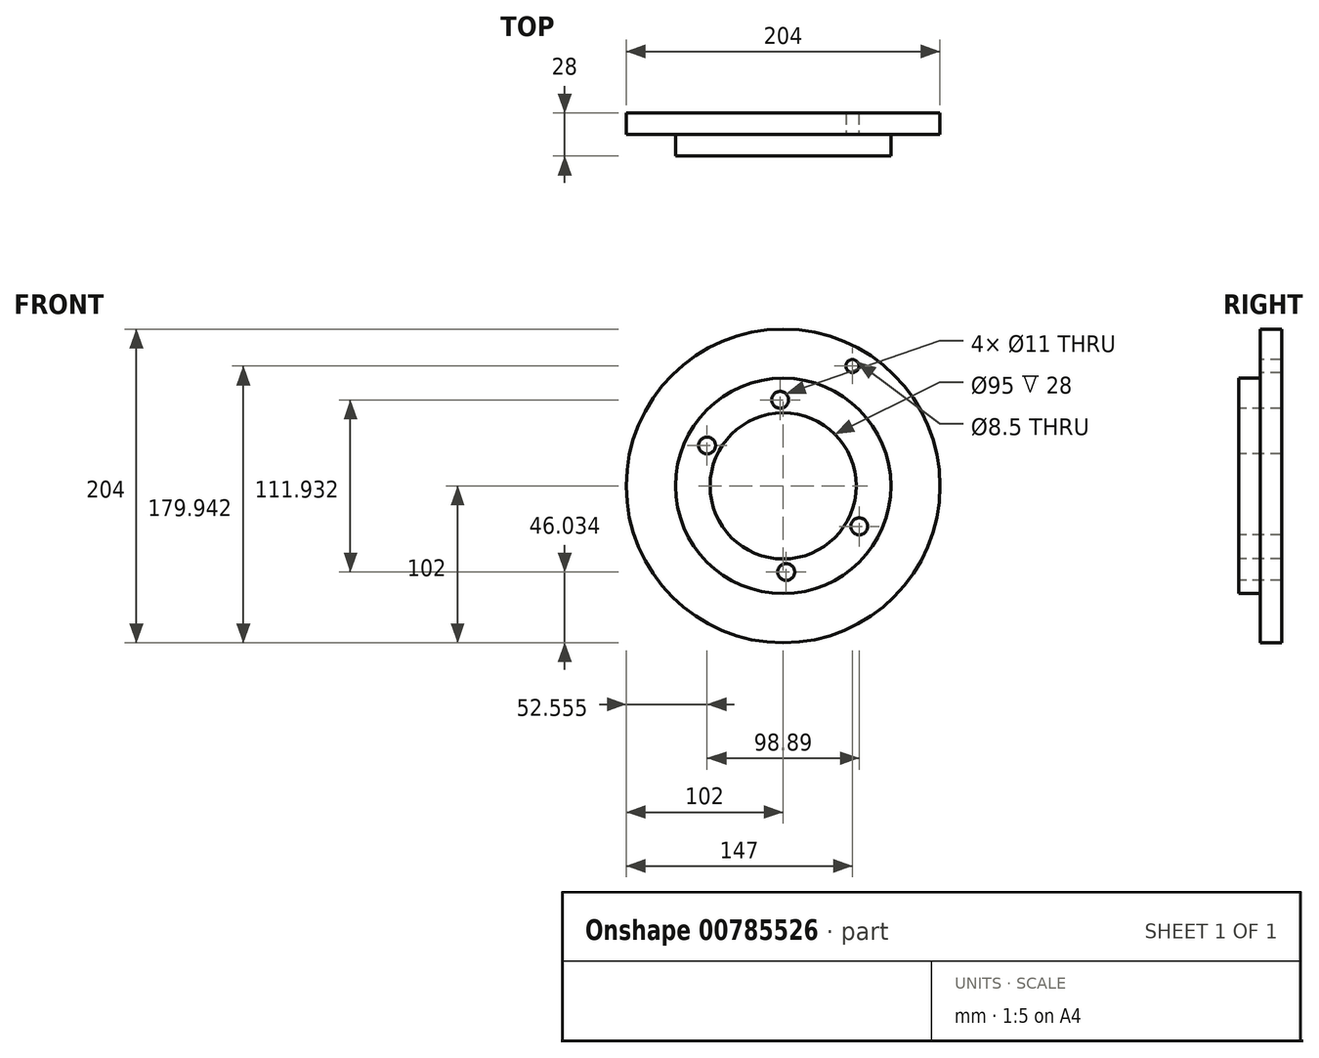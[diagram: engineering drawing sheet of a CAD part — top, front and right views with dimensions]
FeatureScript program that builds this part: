
annotation { "Feature Type Name" : "Feature", "Feature Type Description" : "" }
export const myFeature = defineFeature(function(context is Context, id is Id, definition is map)
    precondition{}
    {
        {
            var Q0;
            Q0=qCreatedBy(makeId("Front.planeOp"),FACE);
            var sketch = newSketch(context, id + "F0", { "sketchPlane" : qUnion([Q0])});
            skCircle(sketch, "E0", {"center": v(0, 0) * mm, "radius": 102 * mm});
            skSolve(sketch);
        }
        {
            var Q0;
            Q0=makeQuery(id+"F0.imprint","IMPRINT",FACE,{"disambiguationData":[TD([[makeQuery(id+"F0.imprint","IMPRINT",EDGE,{"derivedFrom":sQuery(id+"F0.wireOp",EDGE,"E0")}),1.0]])]});
            extrude(context, id + "F1", {"entities" : qUnion([Q0]), "depth" : 14 * mm, "offsetDistance" : 25 * mm});
        }
        {
            var Q0;
            Q0=makeQuery(id+"F1.opExtrude","CAP_FACE",FACE,{"disambiguationData":[OSD([sQuery(id+"F0.wireOp",EDGE,"E0")])],"isStart":false});
            var sketch = newSketch(context, id + "F2", { "sketchPlane" : qUnion([Q0])});
            skCircle(sketch, "E1", {"center": v(0, 0) * mm, "radius": 47.5 * mm});
            skSolve(sketch);
        }
        {
            var Q0;
            Q0=makeQuery(id+"F2.imprint","IMPRINT",FACE,{"disambiguationData":[TD([[makeQuery(id+"F2.imprint","IMPRINT",EDGE,{"derivedFrom":sQuery(id+"F2.wireOp",EDGE,"E1")}),1.0]])]});
            extrude(context, id + "F3", {"entities" : qUnion([Q0]), "operationType" : NewBodyOperationType.REMOVE, "endBound" : BoundingType.THROUGH_ALL, "oppositeDirection" : true, "depth" : 25 * mm, "offsetDistance" : 25 * mm});
        }
        {
            var Q0;
            Q0=makeQuery(id+"F1.opExtrude","CAP_FACE",FACE,{"disambiguationData":[OSD([sQuery(id+"F0.wireOp",EDGE,"E0")])],"isStart":false});
            var sketch = newSketch(context, id + "F4", { "sketchPlane" : qUnion([Q0])});
            skCircle(sketch, "E2", {"center": v(0, 0) * mm, "radius": 56 * mm, "construction": true});
            skLineSegment(sketch, "E3", {"start": v(1.95, -55.97) * mm, "end": v(-1.95, 55.97) * mm, "construction": true});
            skLineSegment(sketch, "E4", {"start": v(0, 0) * mm, "end": v(0, 56) * mm});
            skLineSegment(sketch, "E5", {"start": v(0, 0) * mm, "end": v(-49.45, 26.3) * mm, "construction": true});
            skLineSegment(sketch, "E6", {"start": v(0, 0) * mm, "end": v(49.45, -26.3) * mm, "construction": true});
            skSolve(sketch);
        }
        {
            var Q0;
            Q0=sQuery(id+"F4.wireOp",VERTEX,"E5.end");
            var Q1;
            Q1=sQuery(id+"F4.wireOp",VERTEX,"E3.end");
            var Q2;
            Q2=sQuery(id+"F4.wireOp",VERTEX,"E3.start");
            var Q3;
            Q3=sQuery(id+"F4.wireOp",VERTEX,"E6.end");
            var Q4;
            Q4=makeQuery(id+"F1.opExtrude","SWEPT_BODY",BODY,{"disambiguationData":[OSD([sQuery(id+"F0.wireOp",EDGE,"E0")])]});
            hole(context, id + "F5", {"style" : HoleStyle.SIMPLE, "endStyle" : HoleEndStyle.THROUGH, "holeDiameter" : 11 * mm, "majorDiameter" : 5 * mm, "isTappedThrough" : true, "tappedDepth" : 12 * mm, "tapClearance" : 3, "locations" : qUnion([Q0, Q1, Q2, Q3]), "scope" : qUnion([Q4])});
        }
        {
            var Q0;
            Q0=makeQuery(id+"F1.opExtrude","CAP_FACE",FACE,{"disambiguationData":[OSD([sQuery(id+"F0.wireOp",EDGE,"E0")])],"isStart":false});
            var sketch = newSketch(context, id + "F6", { "sketchPlane" : qUnion([Q0])});
            skCircle(sketch, "E7", {"center": v(0, 0) * mm, "radius": 70 * mm});
            skSolve(sketch);
        }
        {
            var Q0;
            Q0=makeQuery(id+"F6.imprint","IMPRINT",FACE,{"disambiguationData":[TD([[makeQuery(id+"F6.imprint","IMPRINT",EDGE,{"derivedFrom":sQuery(id+"F6.wireOp",EDGE,"E7")}),1.0]])]});
            extrude(context, id + "F7", {"entities" : qUnion([Q0]), "operationType" : NewBodyOperationType.ADD, "depth" : 14 * mm, "offsetDistance" : 25 * mm});
        }
        {
            var Q0;
            Q0=makeQuery(id+"F1.opExtrude","CAP_FACE",FACE,{"disambiguationData":[OSD([sQuery(id+"F0.wireOp",EDGE,"E0")])],"isStart":false});
            var sketch = newSketch(context, id + "F8", { "sketchPlane" : qUnion([Q0])});
            skCircle(sketch, "E8", {"center": v(0, 0) * mm, "radius": 90 * mm, "construction": true});
            skLineSegment(sketch, "E9", {"start": v(0, 0) * mm, "end": v(0, 90) * mm, "construction": true});
            skLineSegment(sketch, "E10", {"start": v(0, 0) * mm, "end": v(45, 77.94) * mm, "construction": true});
            skSolve(sketch);
        }
        {
            var Q0;
            Q0=sQuery(id+"F8.wireOp",VERTEX,"E10.end");
            var Q1;
            Q1=makeQuery(id+"F1.opExtrude","SWEPT_BODY",BODY,{"disambiguationData":[OSD([sQuery(id+"F0.wireOp",EDGE,"E0")])]});
            hole(context, id + "F9", {"style" : HoleStyle.SIMPLE, "endStyle" : HoleEndStyle.THROUGH, "standardTappedOrClearance" : lookupTablePath({ "standard" : "ISO", "engagement" : "75%", "pitch" : "1.5 mm", "size" : "M10", "type" : "Tapped" }), "standardBlindInLast" : lookupTablePath({ "standard" : "ISO", "engagement" : "75%", "pitch" : "1.5 mm", "size" : "M10", "type" : "Tapped" }), "holeDiameter" : 8.5 * mm, "majorDiameter" : 10 * mm, "showTappedDepth" : true, "isTappedThrough" : true, "tappedDepth" : 12 * mm, "tapClearance" : 3, "locations" : qUnion([Q0]), "scope" : qUnion([Q1])});
        }
    });
